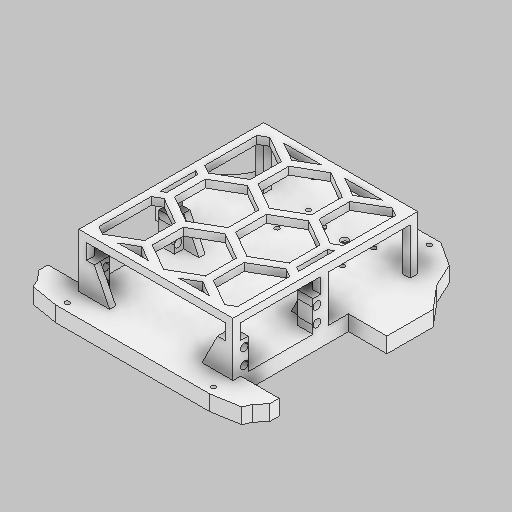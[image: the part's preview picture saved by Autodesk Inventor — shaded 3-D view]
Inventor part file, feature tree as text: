
AUTODESK INVENTOR PART (.ipt)
format: ipt  version: 2025 (Build 290162010, 162A)  size: 1,203,200 bytes
history: native  units: mm
features: other x23, extrude x15, sketch x15
ambient origin geometry x8: Origin, YZ Plane, XZ Plane, XY Plane, X Axis, Y Axis, Z Axis, Center Point
bodies: Body1 (feature_tree)
feature tree (53):
  other  "Sólido1"
  extrude  "Base"  Depth=10.0mm TaperAngle=0.0deg
  extrude  "Llantas"  Depth=70.0mm
  extrude  "Carroceria"  Depth=75.0mm
  extrude  "Tornillos Chasis 1"  Depth=150.0mm
  extrude  "Tornillos Chasis 2"  Depth=10.0mm TaperAngle=0.0deg
  extrude  "Soporte Rueda 1"  Depth=30.0mm
  extrude  "Soporte Rueda 2"  Depth=40.0mm
  extrude  "Soporte Motor 1"  Depth=15.0mm
  extrude  "Soporte Motor 2"  Depth=6.0mm
  extrude  "Soporte Motor 3"  Depth=11.34464mm
  extrude  "Soporte Motor 4"  Depth=5.0mm
  extrude  "Soporte ESP 1"  Depth=5.0mm
  extrude  "Soporte ESP 2"  Depth=37.5mm
  extrude  "Extrusión38"  Depth=5.0mm
  extrude  "Extrusión39"  Depth=10.0mm TaperAngle=0.0deg
  sketch  "Boceto Base"  dims[d44=37.5mm d45=3.0mm]
  sketch  "Boceto Llantas"  dims[d46=5.0mm d47=3.0mm]
  sketch  "Boceto Carroceria"  dims[d48=47.5mm d49=10.0mm d50=0.0mm d81=5.0mm d82=5.0mm d83=5.0mm d84=5.0mm d85=2.0mm d86=0.0mm d244=10.0mm d245=10.0mm d247=10.0mm d248=10.0mm d249=5.0mm d250=42.0mm d251=20.0mm d252=0.0mm d253=5.0mm d254=5.0mm d255=5.0mm d256=5.0mm d257=5.0mm d258=5.0mm d259=10.0mm d260=10.0mm d261=100.0mm d262=0.0mm d263=4.0mm d264=4.0mm d265=10.0mm d266=10.0mm d267=20.0mm d268=0.0mm d269=10.0mm d270=10.0mm d271=100.0mm d272=0.0mm d273=3.0mm d274=35.0mm d275=21.3mm d276=21.3mm d277=3.0mm d278=20.3mm d279=20.0mm d280=0.0mm d281=5.0mm d282=5.0mm d283=5.0mm d284=5.0mm d285=2.0mm d286=0.0mm d287=3.0mm d288=3.0mm d289=50.0mm d290=50.0mm d291=7.5mm d292=7.5mm d293=20.0mm d294=0.0mm d299=5.0mm d300=5.0mm d301=2.0mm d302=0.0mm d303=115.0mm d304=0.0mm d305=5.0mm d306=5.0mm d307=30.0mm d308=0.0mm d329=20.0mm d330=20.0mm d331=120.0deg d332=20.0mm d333=120.0deg d334=20.0mm d335=120.0deg d336=20.0mm d337=120.0deg d338=20.0mm d339=120.0deg d340=0.0mm d341=0.0mm d354=5.0mm d355=0.0mm d64=0.5mm d65=0.872665mm d66=0.5mm d67=0.872665mm d229=0.5mm d230=0.872665mm d231=0.5mm d232=0.872665mm]
  sketch  "Boceto Tornillos Chasis 1"  dims[d0=160.0mm d2=10.0mm d3=0.0mm]
  sketch  "Boceto Tornillos Chasis 2"  dims[d4=70.0mm d5=70.0mm]
  sketch  "Boceto27"  dims[d6=20.0mm d7=75.0mm]
  sketch  "Boceto28"  dims[d8=80.0mm d9=150.0mm]
  sketch  "Boceto29"  dims[d10=25.0mm d11=10.0mm d12=0.0mm]
  sketch  "Boceto30"  dims[d13=30.0mm d14=8.726646mm]
  sketch  "Boceto31"  dims[d15=11.34464mm d16=40.0mm]
  sketch  "Boceto32"  dims[d17=15.0mm d18=15.0mm]
  sketch  "Boceto33"  dims[d19=6.0mm d20=50.0mm]
  sketch  "Boceto35"  dims[d21=8.726646mm d22=11.34464mm]
  sketch  "Boceto36"  dims[d23=6.0mm d24=5.0mm]
  sketch  "Boceto37"  dims[d25=10.0mm d26=0.0mm d43=5.0mm]
  other  "Finish1"
  other  "Finish2"
  other  "Finish3"
  other  "Finish4"
  other  "Finish5"
  other  "Finish6"
  other  "Finish7"
  other  "Finish8"
  other  "Finish9"
  other  "Finish10"
  other  "Finish11"
  other  "Finish12"
  other  "Finish13"
  other  "Finish14"
  other  "Finish15"
  other  "Finish16"
  other  "Finish17"
  other  "Finish18"
  other  "Finish19"
  other  "Finish20"
  other  "Finish21"
  other  "Finish22"
